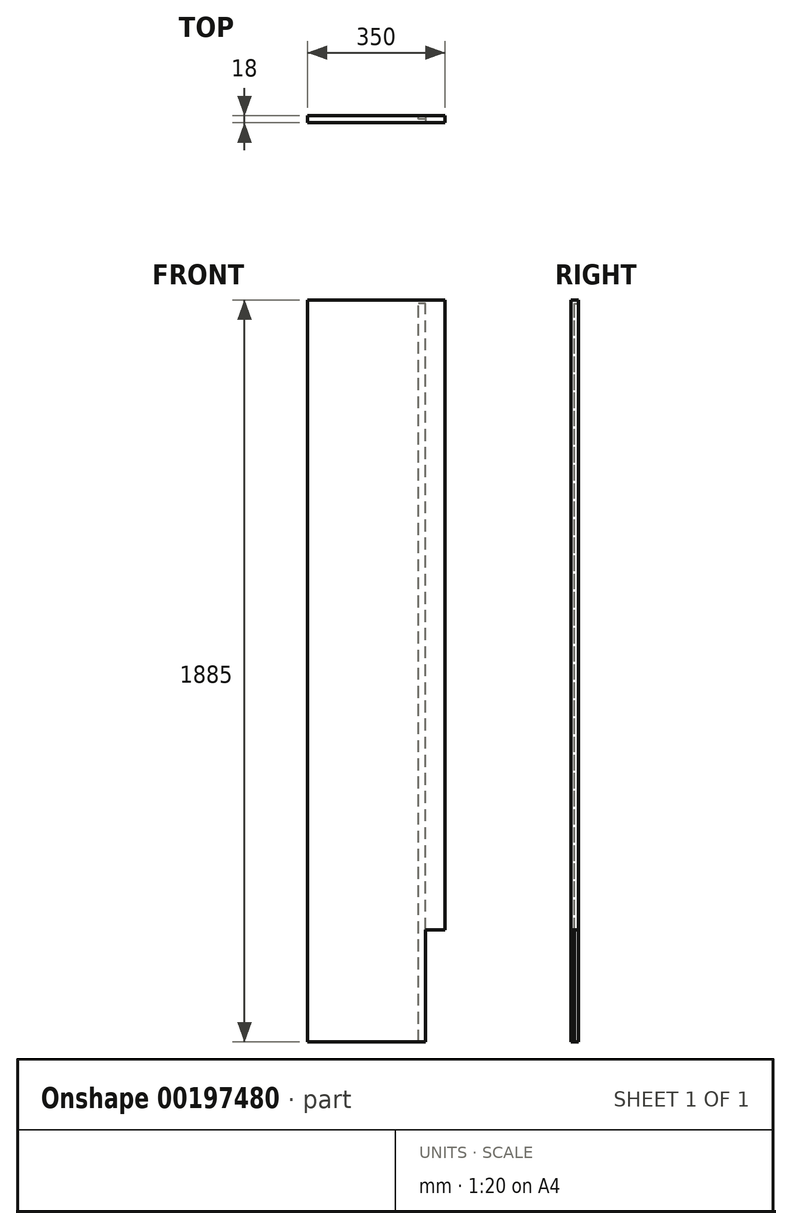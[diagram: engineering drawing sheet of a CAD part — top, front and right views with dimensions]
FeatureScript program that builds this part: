
annotation { "Feature Type Name" : "Feature", "Feature Type Description" : "" }
export const myFeature = defineFeature(function(context is Context, id is Id, definition is map)
    precondition{}
    {
        {
            var Q0;
            Q0=qCreatedBy(makeId("Front.planeOp"),FACE);
            var sketch = newSketch(context, id + "F0", { "sketchPlane" : qUnion([Q0])});
            skLineSegment(sketch, "E0.bottom", {"start": v(175, 942.5) * mm, "end": v(-175, 942.5) * mm});
            skLineSegment(sketch, "E0.top", {"start": v(175, -942.5) * mm, "end": v(-175, -942.5) * mm});
            skLineSegment(sketch, "E0.left", {"start": v(175, 942.5) * mm, "end": v(175, -942.5) * mm});
            skLineSegment(sketch, "E0.right", {"start": v(-175, 942.5) * mm, "end": v(-175, -942.5) * mm});
            skPoint(sketch, "E0.middle", {"position": v(0, 0) * mm});
            skSolve(sketch);
        }
        {
            var Q0;
            Q0 = qSketchRegion(id + "F0", true);
            extrude(context, id + "F1", {"entities" : qUnion([Q0]), "depth" : 18 * mm});
        }
        {
            var Q0;
            Q0=makeQuery(id+"F1.opExtrude","CAP_FACE",FACE,{"disambiguationData":[OSD([sQuery(id+"F0.wireOp",EDGE,"E0.bottom"),sQuery(id+"F0.wireOp",EDGE,"E0.top"),sQuery(id+"F0.wireOp",EDGE,"E0.left"),sQuery(id+"F0.wireOp",EDGE,"E0.right")])],"isStart":false});
            var sketch = newSketch(context, id + "F2", { "sketchPlane" : qUnion([Q0])});
            skLineSegment(sketch, "E1.bottom", {"start": v(175, -942.5) * mm, "end": v(125, -942.5) * mm});
            skLineSegment(sketch, "E1.top", {"start": v(175, -657.5) * mm, "end": v(125, -657.5) * mm});
            skLineSegment(sketch, "E1.left", {"start": v(175, -942.5) * mm, "end": v(175, -657.5) * mm});
            skLineSegment(sketch, "E1.right", {"start": v(125, -942.5) * mm, "end": v(125, -657.5) * mm});
            skSolve(sketch);
        }
        {
            var Q0;
            Q0 = qSketchRegion(id + "F2", true);
            extrude(context, id + "F3", {"entities" : qUnion([Q0]), "operationType" : NewBodyOperationType.REMOVE, "oppositeDirection" : true, "depth" : 18 * mm});
        }
        {
            var Q0;
            Q0=makeQuery(id+"F1.opExtrude","CAP_FACE",FACE,{"disambiguationData":[OSD([sQuery(id+"F0.wireOp",EDGE,"E0.bottom"),sQuery(id+"F0.wireOp",EDGE,"E0.top"),sQuery(id+"F0.wireOp",EDGE,"E0.left"),sQuery(id+"F0.wireOp",EDGE,"E0.right")])],"isStart":true});
            var sketch = newSketch(context, id + "F4", { "sketchPlane" : qUnion([Q0])});
            skLineSegment(sketch, "E2.bottom", {"start": v(-125, -942.5) * mm, "end": v(-107, -942.5) * mm});
            skLineSegment(sketch, "E2.top", {"start": v(-125, 933.5) * mm, "end": v(-107, 933.5) * mm});
            skLineSegment(sketch, "E2.left", {"start": v(-125, -942.5) * mm, "end": v(-125, 933.5) * mm});
            skLineSegment(sketch, "E2.right", {"start": v(-107, -942.5) * mm, "end": v(-107, 933.5) * mm});
            skSolve(sketch);
        }
        {
            var Q0;
            Q0 = qSketchRegion(id + "F4", true);
            extrude(context, id + "F5", {"entities" : qUnion([Q0]), "operationType" : NewBodyOperationType.REMOVE, "oppositeDirection" : true, "depth" : 9 * mm});
        }
    });
